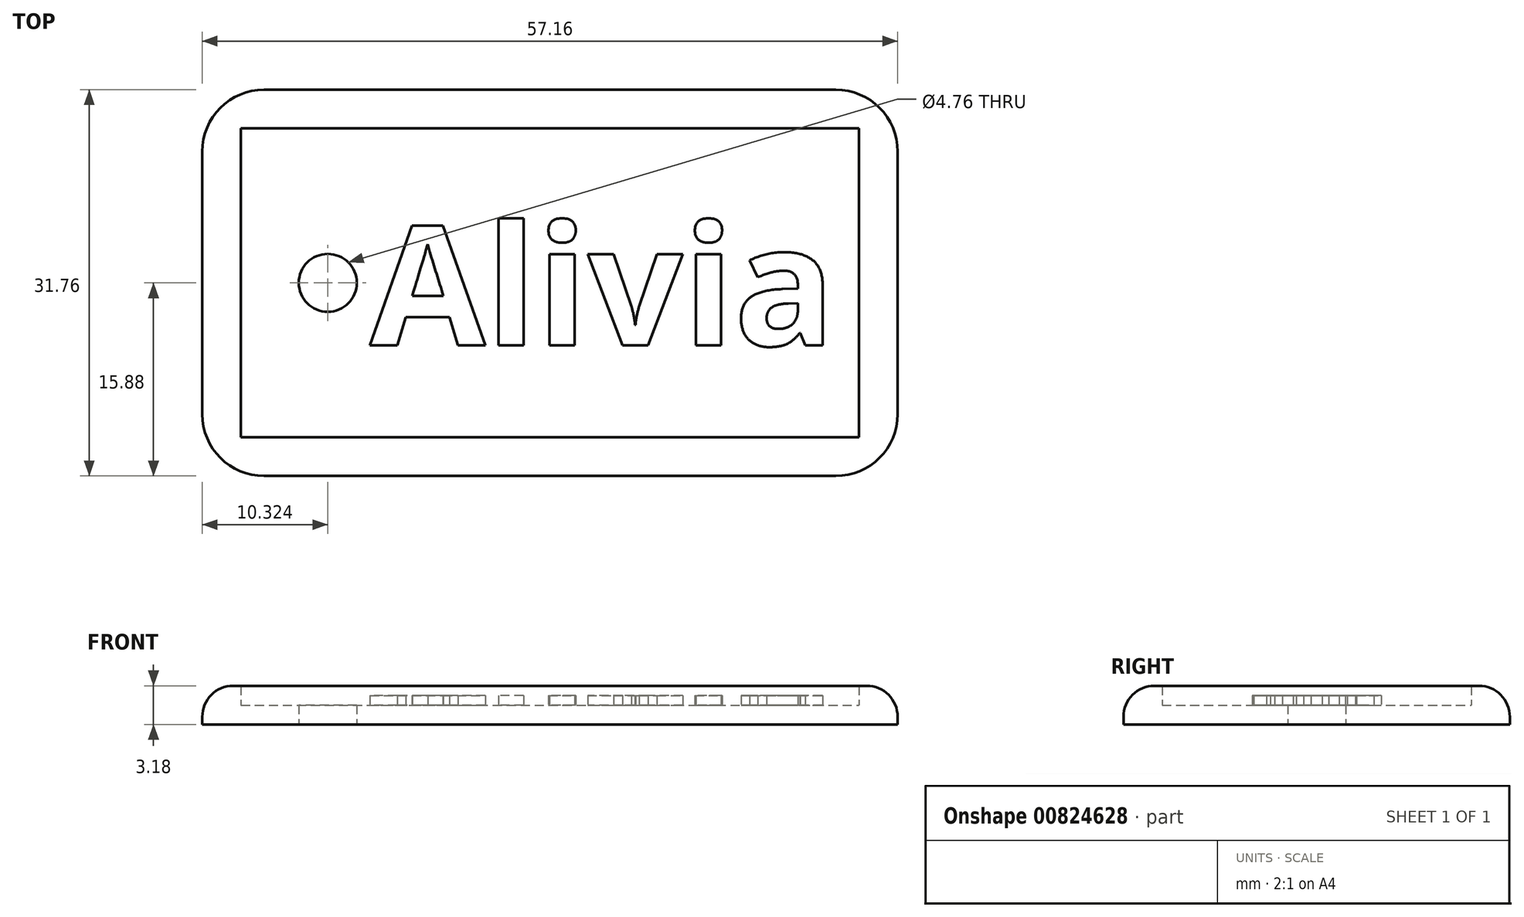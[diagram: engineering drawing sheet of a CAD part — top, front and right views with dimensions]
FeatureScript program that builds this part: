
annotation { "Feature Type Name" : "Feature", "Feature Type Description" : "" }
export const myFeature = defineFeature(function(context is Context, id is Id, definition is map)
    precondition{}
    {
        {
            var Q0;
            Q0=qCreatedBy(makeId("Top.planeOp"),FACE);
            var sketch = newSketch(context, id + "F0", { "sketchPlane" : qUnion([Q0])});
            skLineSegment(sketch, "E0.bottom", {"start": v(0, 0) * mm, "end": v(50.8, 0) * mm});
            skLineSegment(sketch, "E0.top", {"start": v(0, 25.4) * mm, "end": v(50.8, 25.4) * mm});
            skLineSegment(sketch, "E0.left", {"start": v(0, 0) * mm, "end": v(0, 25.4) * mm});
            skLineSegment(sketch, "E0.right", {"start": v(50.8, 0) * mm, "end": v(50.8, 25.4) * mm});
            skCircle(sketch, "E1", {"center": v(7.14, 12.7) * mm, "radius": 2.38 * mm});
            skPoint(sketch, "E1.centerSnap0", {"position": v(0, 12.7) * mm});
            skLineSegment(sketch, "E2.0", {"start": v(-3.18, 28.58) * mm, "end": v(53.97, 28.58) * mm});
            skLineSegment(sketch, "E2.1", {"start": v(-3.17, -3.17) * mm, "end": v(-3.18, 28.58) * mm});
            skLineSegment(sketch, "E2.2", {"start": v(-3.17, -3.17) * mm, "end": v(53.98, -3.17) * mm});
            skLineSegment(sketch, "E2.3", {"start": v(53.98, -3.17) * mm, "end": v(53.97, 28.58) * mm});
            skSolve(sketch);
        }
        {
            var Q0;
            Q0=makeQuery(id+"F0.imprint","IMPRINT",FACE,{"disambiguationData":[TD([[makeQuery(id+"F0.imprint","IMPRINT",EDGE,{"derivedFrom":sQuery(id+"F0.wireOp",EDGE,"E0.bottom")}),1.0]])]});
            extrude(context, id + "F1", {"entities" : qUnion([Q0]), "depth" : 1.59 * mm, "offsetDistance" : 25.4 * mm});
        }
        {
            var Q0;
            Q0 = qSketchRegion(id + "F0", true);
            extrude(context, id + "F2", {"entities" : qUnion([Q0]), "operationType" : NewBodyOperationType.ADD, "depth" : 3.17 * mm, "offsetDistance" : 25.4 * mm});
        }
        {
            var Q0;
            Q0=makeQuery(id+"F2.opExtrude","SWEPT_EDGE",EDGE,{"disambiguationData":[OSD([sQuery(id+"F0.wireOp",EDGE,"E2.2"),sQuery(id+"F0.wireOp",EDGE,"E2.3")])]});
            var Q1;
            Q1=makeQuery(id+"F2.opExtrude","SWEPT_EDGE",EDGE,{"disambiguationData":[OSD([sQuery(id+"F0.wireOp",EDGE,"E2.1"),sQuery(id+"F0.wireOp",EDGE,"E2.2")])]});
            var Q2;
            Q2=makeQuery(id+"F2.opExtrude","SWEPT_EDGE",EDGE,{"disambiguationData":[OSD([sQuery(id+"F0.wireOp",EDGE,"E2.0"),sQuery(id+"F0.wireOp",EDGE,"E2.3")])]});
            var Q3;
            Q3=makeQuery(id+"F2.opExtrude","SWEPT_EDGE",EDGE,{"disambiguationData":[OSD([sQuery(id+"F0.wireOp",EDGE,"E2.0"),sQuery(id+"F0.wireOp",EDGE,"E2.1")])]});
            fillet(context, id + "F3", {"entities" : qUnion([Q0, Q1, Q2, Q3]), "radius" : 5.08 * mm, "tangentPropagation" : true, "allowEdgeOverflow" : false});
        }
        {
            var Q0;
            Q0=makeQuery(id+"F2.opExtrude","CAP_EDGE",EDGE,{"disambiguationData":[OSD([sQuery(id+"F0.wireOp",EDGE,"E2.2")])],"isStart":false});
            fillet(context, id + "F4", {"entities" : qUnion([Q0]), "radius" : 2.54 * mm, "tangentPropagation" : true, "allowEdgeOverflow" : false});
        }
        {
            var Q0;
            Q0=makeQuery(id+"F1.opExtrude","CAP_FACE",FACE,{"disambiguationData":[OSD([sQuery(id+"F0.wireOp",EDGE,"E0.bottom"),sQuery(id+"F0.wireOp",EDGE,"E0.top"),sQuery(id+"F0.wireOp",EDGE,"E0.left"),sQuery(id+"F0.wireOp",EDGE,"E0.right"),sQuery(id+"F0.wireOp",EDGE,"E1")])],"isStart":false});
            var sketch = newSketch(context, id + "F5", { "sketchPlane" : qUnion([Q0])});
            skSolve(sketch);
        }
        {
            var Q0;
            Q0=makeQuery(id+"F5.imprint","IMPRINT",FACE,{"disambiguationData":[TD([[makeQuery(id+"F5.imprint","IMPRINT",EDGE,{"derivedFrom":makeQuery(id+"F1.opExtrude","CAP_EDGE",EDGE,{"disambiguationData":[OSD([sQuery(id+"F0.wireOp",EDGE,"E1")])],"isStart":false})}),-1.0]])]});
            var sketch = newSketch(context, id + "F6", { "sketchPlane" : qUnion([Q0])});
            skText(sketch, "E3", { "text": "Alivia", "fontName": "OpenSans-Bold.ttf"});
            const initialGuessF6  = {"E3": [0.0106, 0.00755, 1, 0, 0.00991]};
            skSetInitialGuess(sketch, initialGuessF6);
            skSolve(sketch);
        }
        {
            var Q0;
            Q0 = qSketchRegion(id + "F6", true);
            extrude(context, id + "F7", {"entities" : qUnion([Q0]), "operationType" : NewBodyOperationType.ADD, "depth" : 0.8 * mm, "offsetDistance" : 25.4 * mm});
        }
    });
